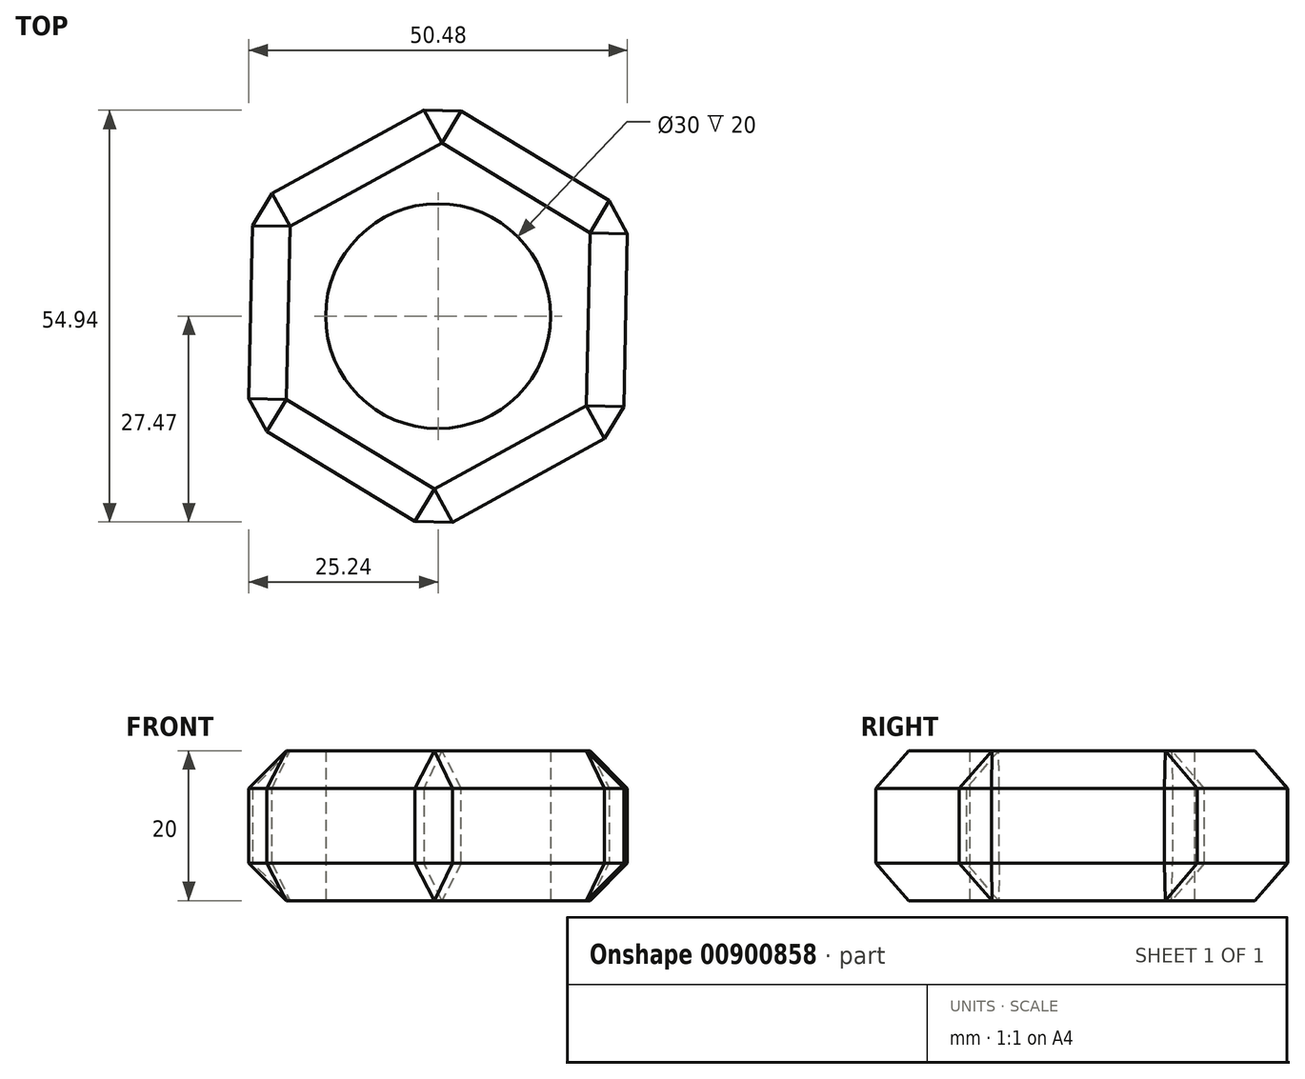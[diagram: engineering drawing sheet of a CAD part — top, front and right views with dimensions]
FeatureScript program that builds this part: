
annotation { "Feature Type Name" : "Feature", "Feature Type Description" : "" }
export const myFeature = defineFeature(function(context is Context, id is Id, definition is map)
    precondition{}
    {
        {
            var Q0;
            Q0=qCreatedBy(makeId("Top.planeOp"),FACE);
            var sketch = newSketch(context, id + "F0", { "sketchPlane" : qUnion([Q0])});
            skCircle(sketch, "E0.cCircle", {"center": v(0, 0) * mm, "radius": 25 * mm, "construction": true});
            skLineSegment(sketch, "E0.0", {"start": v(-24.69, 14.97) * mm, "end": v(0.62, 28.86) * mm});
            skLineSegment(sketch, "E0.1", {"start": v(0.62, 28.86) * mm, "end": v(25.3, 13.9) * mm});
            skLineSegment(sketch, "E0.2", {"start": v(25.3, 13.9) * mm, "end": v(24.69, -14.97) * mm});
            skLineSegment(sketch, "E0.3", {"start": v(24.69, -14.97) * mm, "end": v(-0.62, -28.86) * mm});
            skLineSegment(sketch, "E0.4", {"start": v(-0.62, -28.86) * mm, "end": v(-25.3, -13.9) * mm});
            skLineSegment(sketch, "E0.5", {"start": v(-25.3, -13.9) * mm, "end": v(-24.69, 14.97) * mm});
            skPoint(sketch, "E0.0.midPoint", {"position": v(-12.03, 21.91) * mm});
            skSolve(sketch);
        }
        {
            var Q0;
            Q0=makeQuery(id+"F0.imprint","IMPRINT",FACE,{"disambiguationData":[TD([[makeQuery(id+"F0.imprint","IMPRINT",EDGE,{"derivedFrom":sQuery(id+"F0.wireOp",EDGE,"E0.0")}),-1.0]])]});
            extrude(context, id + "F1", {"entities" : qUnion([Q0]), "depth" : 20 * mm, "offsetDistance" : 25 * mm});
        }
        {
            var Q0;
            Q0=qCreatedBy(makeId("Top.planeOp"),FACE);
            var sketch = newSketch(context, id + "F2", { "sketchPlane" : qUnion([Q0])});
            skCircle(sketch, "E1", {"center": v(0, 0) * mm, "radius": 15 * mm});
            skSolve(sketch);
        }
        {
            var Q0;
            Q0=makeQuery(id+"F2.imprint","IMPRINT",FACE,{"disambiguationData":[TD([[makeQuery(id+"F2.imprint","IMPRINT",EDGE,{"derivedFrom":sQuery(id+"F2.wireOp",EDGE,"E1")}),1.0]])]});
            extrude(context, id + "F3", {"entities" : qUnion([Q0]), "operationType" : NewBodyOperationType.REMOVE, "depth" : 25 * mm, "offsetDistance" : 25 * mm});
        }
        {
            var Q0;
            Q0=makeQuery(id+"F1.opExtrude","CAP_EDGE",EDGE,{"disambiguationData":[OSD([sQuery(id+"F0.wireOp",EDGE,"E0.0")])],"isStart":false});
            var Q1;
            Q1=makeQuery(id+"F1.opExtrude","CAP_EDGE",EDGE,{"disambiguationData":[OSD([sQuery(id+"F0.wireOp",EDGE,"E0.1")])],"isStart":false});
            var Q2;
            Q2=makeQuery(id+"F1.opExtrude","CAP_EDGE",EDGE,{"disambiguationData":[OSD([sQuery(id+"F0.wireOp",EDGE,"E0.2")])],"isStart":false});
            var Q3;
            Q3=makeQuery(id+"F1.opExtrude","CAP_EDGE",EDGE,{"disambiguationData":[OSD([sQuery(id+"F0.wireOp",EDGE,"E0.3")])],"isStart":false});
            var Q4;
            Q4=makeQuery(id+"F1.opExtrude","CAP_EDGE",EDGE,{"disambiguationData":[OSD([sQuery(id+"F0.wireOp",EDGE,"E0.4")])],"isStart":false});
            var Q5;
            Q5=makeQuery(id+"F1.opExtrude","CAP_EDGE",EDGE,{"disambiguationData":[OSD([sQuery(id+"F0.wireOp",EDGE,"E0.5")])],"isStart":false});
            var Q6;
            Q6=makeQuery(id+"F1.opExtrude","CAP_EDGE",EDGE,{"disambiguationData":[OSD([sQuery(id+"F0.wireOp",EDGE,"E0.0")])],"isStart":true});
            var Q7;
            Q7=makeQuery(id+"F1.opExtrude","CAP_EDGE",EDGE,{"disambiguationData":[OSD([sQuery(id+"F0.wireOp",EDGE,"E0.5")])],"isStart":true});
            var Q8;
            Q8=makeQuery(id+"F1.opExtrude","CAP_EDGE",EDGE,{"disambiguationData":[OSD([sQuery(id+"F0.wireOp",EDGE,"E0.4")])],"isStart":true});
            var Q9;
            Q9=makeQuery(id+"F1.opExtrude","CAP_EDGE",EDGE,{"disambiguationData":[OSD([sQuery(id+"F0.wireOp",EDGE,"E0.3")])],"isStart":true});
            var Q10;
            Q10=makeQuery(id+"F1.opExtrude","CAP_EDGE",EDGE,{"disambiguationData":[OSD([sQuery(id+"F0.wireOp",EDGE,"E0.2")])],"isStart":true});
            var Q11;
            Q11=makeQuery(id+"F1.opExtrude","CAP_EDGE",EDGE,{"disambiguationData":[OSD([sQuery(id+"F0.wireOp",EDGE,"E0.1")])],"isStart":true});
            var Q12;
            Q12=makeQuery(id+"F1.opExtrude","SWEPT_EDGE",EDGE,{"disambiguationData":[OSD([sQuery(id+"F0.wireOp",EDGE,"E0.0"),sQuery(id+"F0.wireOp",EDGE,"E0.1")])]});
            var Q13;
            Q13=makeQuery(id+"F1.opExtrude","SWEPT_EDGE",EDGE,{"disambiguationData":[OSD([sQuery(id+"F0.wireOp",EDGE,"E0.1"),sQuery(id+"F0.wireOp",EDGE,"E0.2")])]});
            var Q14;
            Q14=makeQuery(id+"F1.opExtrude","SWEPT_EDGE",EDGE,{"disambiguationData":[OSD([sQuery(id+"F0.wireOp",EDGE,"E0.3"),sQuery(id+"F0.wireOp",EDGE,"E0.4")])]});
            var Q15;
            Q15=makeQuery(id+"F1.opExtrude","SWEPT_EDGE",EDGE,{"disambiguationData":[OSD([sQuery(id+"F0.wireOp",EDGE,"E0.4"),sQuery(id+"F0.wireOp",EDGE,"E0.5")])]});
            var Q16;
            Q16=makeQuery(id+"F1.opExtrude","SWEPT_EDGE",EDGE,{"disambiguationData":[OSD([sQuery(id+"F0.wireOp",EDGE,"E0.2"),sQuery(id+"F0.wireOp",EDGE,"E0.3")])]});
            var Q17;
            Q17=makeQuery(id+"F1.opExtrude","SWEPT_EDGE",EDGE,{"disambiguationData":[OSD([sQuery(id+"F0.wireOp",EDGE,"E0.0"),sQuery(id+"F0.wireOp",EDGE,"E0.5")])]});
            chamfer(context, id + "F4", {"entities" : qUnion([Q0, Q1, Q2, Q3, Q4, Q5, Q6, Q7, Q8, Q9, Q10, Q11, Q12, Q13, Q14, Q15, Q16, Q17]), "width" : 5 * mm, "tangentPropagation" : true});
        }
    });
